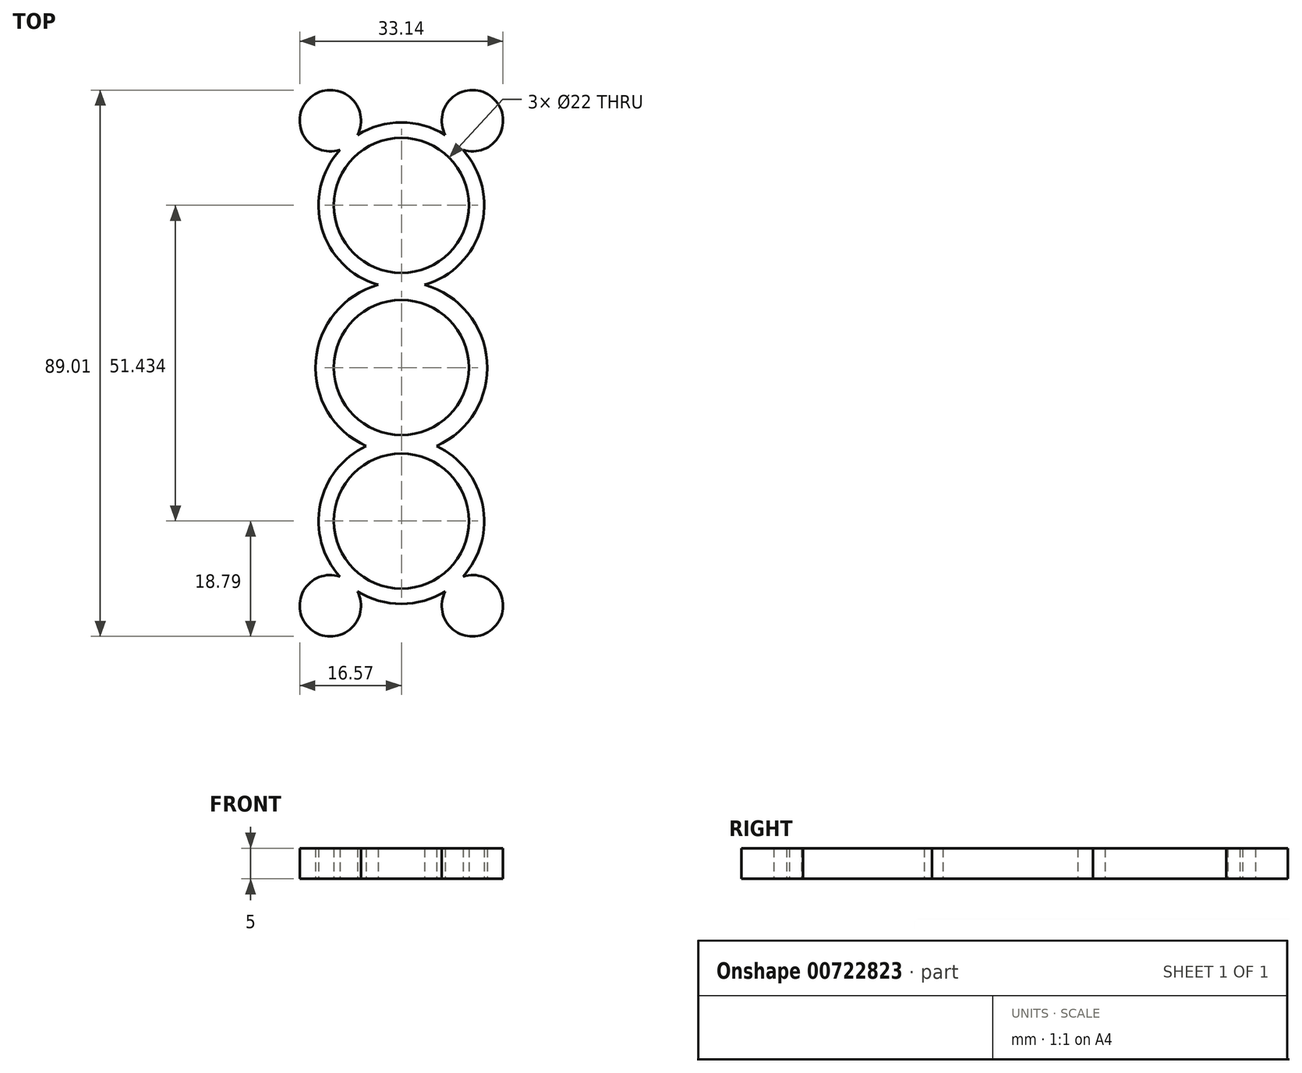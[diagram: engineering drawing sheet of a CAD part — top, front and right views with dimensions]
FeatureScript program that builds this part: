
annotation { "Feature Type Name" : "Feature", "Feature Type Description" : "" }
export const myFeature = defineFeature(function(context is Context, id is Id, definition is map)
    precondition{}
    {
        {
            var Q0;
            Q0=qCreatedBy(makeId("Top.planeOp"),FACE);
            var sketch = newSketch(context, id + "F0", { "sketchPlane" : qUnion([Q0])});
            skCircle(sketch, "E0", {"center": v(0, 0) * mm, "radius": 11 * mm});
            skCircle(sketch, "E1", {"center": v(0, 26.43) * mm, "radius": 11 * mm});
            skArc(sketch, "E2", {"start": v(3.79, 13.48) * mm, "mid": v(12.99, 22.75) * mm, "end": v(10.04, 35.46) * mm});
            skArc(sketch, "E3", {"start": v(-3.79, 13.48) * mm, "mid": v(-13.96, 1.03) * mm, "end": v(-5.73, -12.78) * mm});
            skCircle(sketch, "E4", {"center": v(0, -25) * mm, "radius": 11 * mm});
            skArc(sketch, "E5", {"start": v(-5.73, -12.78) * mm, "mid": v(-13.23, -22.32) * mm, "end": v(-10.04, -34.03) * mm});
            skArc(sketch, "E6.trimOffspring", {"start": v(5.73, -12.78) * mm, "mid": v(13.96, 1.03) * mm, "end": v(3.79, 13.48) * mm});
            skArc(sketch, "E7", {"start": v(-7.15, 37.89) * mm, "mid": v(-14.78, 44.05) * mm, "end": v(-10.04, 35.46) * mm});
            skArc(sketch, "E8", {"start": v(10.04, 35.46) * mm, "mid": v(14.78, 44.05) * mm, "end": v(7.15, 37.89) * mm});
            skArc(sketch, "E9", {"start": v(-10.04, -34.03) * mm, "mid": v(-14.78, -42.62) * mm, "end": v(-7.15, -36.45) * mm});
            skArc(sketch, "E10", {"start": v(7.15, -36.45) * mm, "mid": v(14.78, -42.62) * mm, "end": v(10.04, -34.03) * mm});
            skArc(sketch, "E11.trimOffspring", {"start": v(-10.04, 35.46) * mm, "mid": v(-12.99, 22.75) * mm, "end": v(-3.79, 13.48) * mm});
            skArc(sketch, "E12.trimOffspring", {"start": v(7.15, 37.89) * mm, "mid": v(0, 39.93) * mm, "end": v(-7.15, 37.89) * mm});
            skArc(sketch, "E13.trimOffspring", {"start": v(-7.15, -36.45) * mm, "mid": v(0, -38.5) * mm, "end": v(7.15, -36.45) * mm});
            skArc(sketch, "E14.trimOffspring", {"start": v(10.04, -34.03) * mm, "mid": v(13.23, -22.32) * mm, "end": v(5.73, -12.78) * mm});
            skSolve(sketch);
        }
        {
            var Q0;
            Q0=makeQuery(id+"F0.imprint","IMPRINT",FACE,{"disambiguationData":[TD([[makeQuery(id+"F0.imprint","IMPRINT",EDGE,{"derivedFrom":sQuery(id+"F0.wireOp",EDGE,"E1")}),-1.0]])]});
            extrude(context, id + "F1", {"entities" : qUnion([Q0]), "depth" : 5 * mm, "offsetDistance" : 25 * mm});
        }
    });
